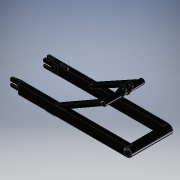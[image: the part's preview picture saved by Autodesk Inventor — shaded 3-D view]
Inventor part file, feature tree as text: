
AUTODESK INVENTOR PART (.ipt)
format: ipt  version: 2019.3 (Build 233278000, 278)  size: 369,152 bytes
history: native  units: mm
features: other x11, reference x2, plane x1, extrude x1, fillet x1, sketch x1
ambient origin geometry x8: Origin, YZ Plane, XZ Plane, XY Plane, X Axis, Y Axis, Z Axis, Center Point
bodies: Solid1 (feature_tree), Solid2 (feature_tree), Solid3 (feature_tree), Solid4 (feature_tree), Solid5 (feature_tree)
feature tree (17):
  other  "Swingarm.ipt"
  plane  "Work Plane1"
  extrude  "Extrusion1"  Depth=6.0mm
  fillet  "Fillet1"  Radius=6.0mm
  other  "Arms::Swingarm.ipt"
  other  "ShockPlate::Swingarm.ipt"
  other  "Dropout::Swingarm.ipt"
  other  "BrakePlate::Swingarm.ipt"
  other  "PivotCup::Swingarm.ipt"
  other  "TaggingFeature1"
  sketch  "Sketch1"  dims[d0=10.0mm d1=6.0mm d2=6.0mm d3=25.495492mm d4=25.495492mm d5=3.0mm d6=0.0mm d7=12.0mm]
  reference  "Reference2"
  reference  "Reference3"
  other  "ChainGuideTab"
  other  "<userpath>\Desktop\3dprojects\OpenEmoto\OpenEmoto.iam"
  other  "OpenEmoto.iam"
  other  "ChainGuide:1"
